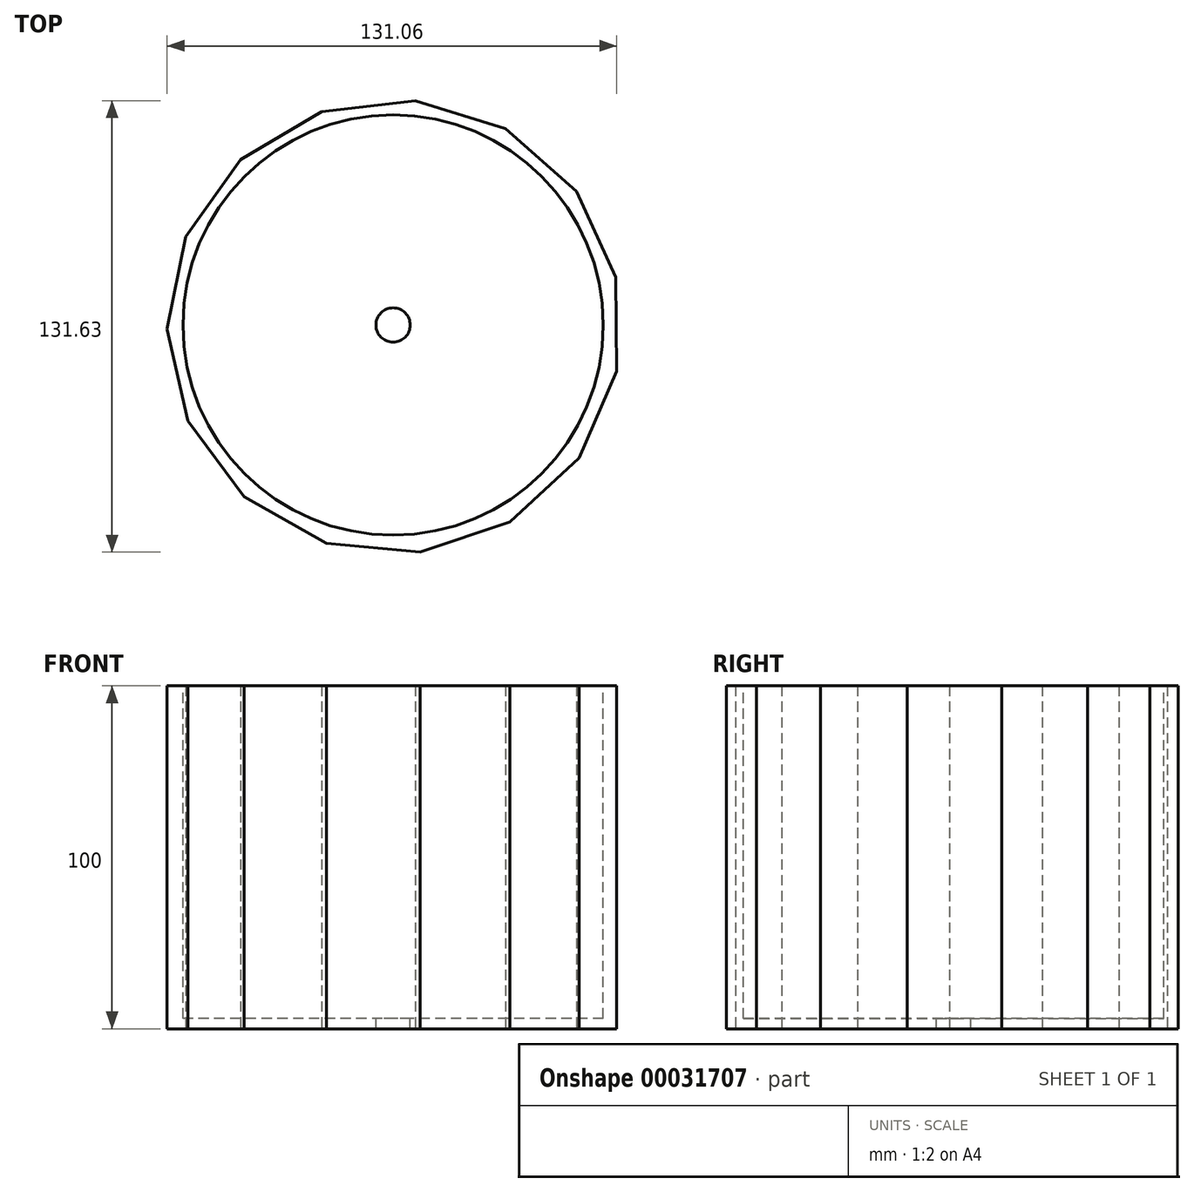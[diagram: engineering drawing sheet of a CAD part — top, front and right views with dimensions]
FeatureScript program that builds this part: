
annotation { "Feature Type Name" : "Feature", "Feature Type Description" : "" }
export const myFeature = defineFeature(function(context is Context, id is Id, definition is map)
    precondition{}
    {
        {
            var Q0;
            Q0=qCreatedBy(makeId("Top.planeOp"),FACE);
            var sketch = newSketch(context, id + "F0", { "sketchPlane" : qUnion([Q0])});
            skCircle(sketch, "E0.cCircle", {"center": v(0.31, -0.47) * mm, "radius": 64.74 * mm, "construction": true});
            skLineSegment(sketch, "E0.0", {"start": v(-20.81, 62.25) * mm, "end": v(6.52, 65.42) * mm});
            skLineSegment(sketch, "E0.1", {"start": v(6.52, 65.42) * mm, "end": v(32.79, 57.2) * mm});
            skLineSegment(sketch, "E0.2", {"start": v(32.79, 57.2) * mm, "end": v(53.43, 39) * mm});
            skLineSegment(sketch, "E0.3", {"start": v(53.43, 39) * mm, "end": v(64.9, 13.99) * mm});
            skLineSegment(sketch, "E0.4", {"start": v(64.9, 13.99) * mm, "end": v(65.19, -13.53) * mm});
            skLineSegment(sketch, "E0.5", {"start": v(65.19, -13.53) * mm, "end": v(54.27, -38.8) * mm});
            skLineSegment(sketch, "E0.6", {"start": v(54.27, -38.8) * mm, "end": v(34.01, -57.42) * mm});
            skLineSegment(sketch, "E0.7", {"start": v(34.01, -57.42) * mm, "end": v(7.93, -66.2) * mm});
            skLineSegment(sketch, "E0.8", {"start": v(7.93, -66.2) * mm, "end": v(-19.47, -63.62) * mm});
            skLineSegment(sketch, "E0.9", {"start": v(-19.47, -63.62) * mm, "end": v(-43.44, -50.12) * mm});
            skLineSegment(sketch, "E0.10", {"start": v(-43.44, -50.12) * mm, "end": v(-59.86, -28.03) * mm});
            skLineSegment(sketch, "E0.11", {"start": v(-59.86, -28.03) * mm, "end": v(-65.87, -1.17) * mm});
            skLineSegment(sketch, "E0.12", {"start": v(-65.87, -1.17) * mm, "end": v(-60.43, 25.8) * mm});
            skLineSegment(sketch, "E0.13", {"start": v(-60.43, 25.8) * mm, "end": v(-44.5, 48.24) * mm});
            skLineSegment(sketch, "E0.14", {"start": v(-44.5, 48.24) * mm, "end": v(-20.81, 62.25) * mm});
            skPoint(sketch, "E0.0.midPoint", {"position": v(-7.14, 63.84) * mm});
            skSolve(sketch);
        }
        {
            var Q0;
            Q0=makeQuery(id+"F0.imprint","IMPRINT",FACE,{"disambiguationData":[TD([[makeQuery(id+"F0.imprint","IMPRINT",EDGE,{"derivedFrom":sQuery(id+"F0.wireOp",EDGE,"E0.0")}),-1.0]])]});
            extrude(context, id + "F1", {"entities" : qUnion([Q0]), "depth" : 100 * mm});
        }
        {
            var Q0;
            Q0=makeQuery(id+"F1.opExtrude","CAP_FACE",FACE,{"disambiguationData":[OSD([sQuery(id+"F0.wireOp",EDGE,"E0.0"),sQuery(id+"F0.wireOp",EDGE,"E0.1"),sQuery(id+"F0.wireOp",EDGE,"E0.2"),sQuery(id+"F0.wireOp",EDGE,"E0.3"),sQuery(id+"F0.wireOp",EDGE,"E0.4"),sQuery(id+"F0.wireOp",EDGE,"E0.5"),sQuery(id+"F0.wireOp",EDGE,"E0.6"),sQuery(id+"F0.wireOp",EDGE,"E0.7"),sQuery(id+"F0.wireOp",EDGE,"E0.8"),sQuery(id+"F0.wireOp",EDGE,"E0.9"),sQuery(id+"F0.wireOp",EDGE,"E0.10"),sQuery(id+"F0.wireOp",EDGE,"E0.11"),sQuery(id+"F0.wireOp",EDGE,"E0.12"),sQuery(id+"F0.wireOp",EDGE,"E0.13"),sQuery(id+"F0.wireOp",EDGE,"E0.14")])],"isStart":false});
            var sketch = newSketch(context, id + "F2", { "sketchPlane" : qUnion([Q0])});
            skCircle(sketch, "E1", {"center": v(0, 0) * mm, "radius": 61.27 * mm});
            skSolve(sketch);
        }
        {
            var Q0;
            Q0 = qSketchRegion(id + "F2", true);
            extrude(context, id + "F3", {"entities" : qUnion([Q0]), "operationType" : NewBodyOperationType.REMOVE, "oppositeDirection" : true, "depth" : 97 * mm});
        }
        {
            var Q0;
            Q0=makeQuery(id+"F3.boolean.opBoolean","COPY",FACE,{"derivedFrom":makeQuery(id+"F3.opExtrude","CAP_FACE",FACE,{"disambiguationData":[OSD([sQuery(id+"F2.wireOp",EDGE,"E1")])],"isStart":false})});
            var sketch = newSketch(context, id + "F4", { "sketchPlane" : qUnion([Q0])});
            skCircle(sketch, "E2", {"center": v(0, 0) * mm, "radius": 5 * mm});
            skSolve(sketch);
        }
        {
            var Q0;
            Q0=makeQuery(id+"F4.imprint","IMPRINT",FACE,{"disambiguationData":[TD([[makeQuery(id+"F4.imprint","IMPRINT",EDGE,{"derivedFrom":sQuery(id+"F4.wireOp",EDGE,"E2")}),1.0]])]});
            extrude(context, id + "F5", {"entities" : qUnion([Q0]), "operationType" : NewBodyOperationType.REMOVE, "oppositeDirection" : true, "depth" : 25 * mm});
        }
    });
